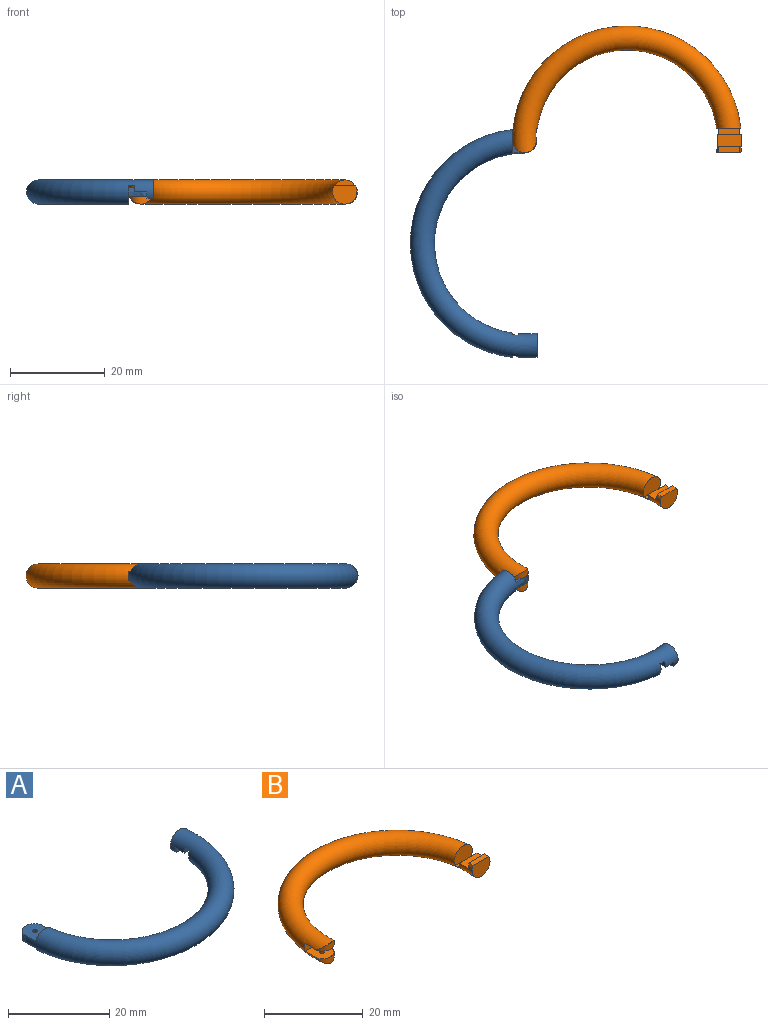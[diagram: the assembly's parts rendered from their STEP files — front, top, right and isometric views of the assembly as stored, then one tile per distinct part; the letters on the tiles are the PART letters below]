
ASSEMBLY  parts=2 mates=1
PART A: 17 faces, bbox 52.4x29.7x5.3 mm
  f0: torus R=21.59mm, axis (0,0,1), area 1048.6mm2, adj f1,f3,f4,f5,f6,f7,f8,f9
  f1: torus R=21.59mm, axis (0,0,1), area 1.7mm2, adj f0,f10,f15,f16
  f2: cylinder r=0.5mm len=1.71mm, axis (0,0,1), area 5.4mm2, adj f6,f9
  f3: plane 0.39x0.01mm, normal (0,1,0), area 0mm2, adj f0,f4
  f4: cylinder r=2.53mm len=5.06mm, axis (0,0,-1), area 12.5mm2, adj f0,f3,f5,f6,f9
  f5: plane 0.43x0.01mm, normal (0,1,0), area 0mm2, adj f0,f4
  f6: plane 5.15x5.03mm, normal (0,0,-1), area 21.4mm2, adj f0,f2,f4,f7
  f7: plane 4.83x1.7mm, normal (0,1,0), area 5.9mm2, adj f0,f6
  f8: plane 4.96x1.83mm, normal (0,1,0), area 5.9mm2, adj f0,f9
  f9: plane 5.15x5.03mm, normal (0,0,1), area 21.4mm2, adj f0,f2,f4,f8
  f10: plane 5.17x3.86mm, normal (0,1,0), area 16.4mm2, adj f0,f1,f16
  f11: plane 5.16x3.86mm, normal (0,1,0), area 16.4mm2, adj f0,f12
  f12: plane 4.53x1.27mm, normal (0,0,-1), area 5.6mm2, adj f0,f11,f13
  f13: plane 5.1x1.28mm, normal (0,-1,0), area 6.2mm2, adj f0,f12,f14
  f14: plane 5.12x2.54mm, normal (0,0,-1), area 12.9mm2, adj f0,f13,f15
  f15: plane 5.1x1.28mm, normal (0,-1,0), area 6.2mm2, adj f0,f1,f14,f16
  f16: plane 4.53x1.27mm, normal (0,0,-1), area 5.6mm2, adj f0,f1,f10,f15
PART B: 15 faces, bbox 52.3x29.7x5.2 mm
  f0: torus R=21.59mm, axis (0,0,1), area 1093.6mm2, adj f2,f3,f4,f5,f6,f7,f8,f9
  f1: cylinder r=0.5mm len=1.91mm, axis (0,0,1), area 6mm2, adj f4,f14
  f2: cylinder r=2.35mm len=4.71mm, axis (0,0,1), area 5.9mm2, adj f0,f4
  f3: cylinder r=2.35mm len=4.71mm, axis (0,0,1), area 5.9mm2, adj f0,f14
  f4: plane 5.17x4.96mm, normal (0,0,-1), area 20.8mm2, adj f0,f1,f2,f13
  f5: torus R=21.59mm, axis (0,0,1), area 1.7mm2, adj f0,f6,f7,f12
  f6: plane 4.53x1.27mm, normal (0,0,1), area 5.6mm2, adj f0,f5,f7,f12
  f7: plane 5.1x1.28mm, normal (0,1,0), area 6.2mm2, adj f0,f5,f6,f8
  f8: plane 5.12x2.54mm, normal (0,0,1), area 12.9mm2, adj f0,f7,f9
  f9: plane 5.09x1.27mm, normal (0,1,0), area 6.2mm2, adj f0,f8,f10
  f10: plane 4.53x1.27mm, normal (0,0,1), area 5.6mm2, adj f0,f9,f11
  f11: plane 5.14x3.84mm, normal (0,-1,0), area 16.4mm2, adj f0,f10
  f12: plane 5.17x3.86mm, normal (0,-1,0), area 16.4mm2, adj f0,f5,f6
  f13: plane 5.19x1.91mm, normal (0,-1,0), area 9.5mm2, adj f0,f4,f14
  f14: plane 5.17x4.96mm, normal (0,0,1), area 20.8mm2, adj f0,f1,f3,f13
PLACE A rot(axis=(0,0,-1),90deg) t=(-26.09,-14.25,-1.06)mm
PLACE B t=(-4.59,7.43,-1.06)mm fixed
MATE fastened B.f1 <-> A.f2  axis (0,0,1) through (-26.18,7.34,-1.06)mm
